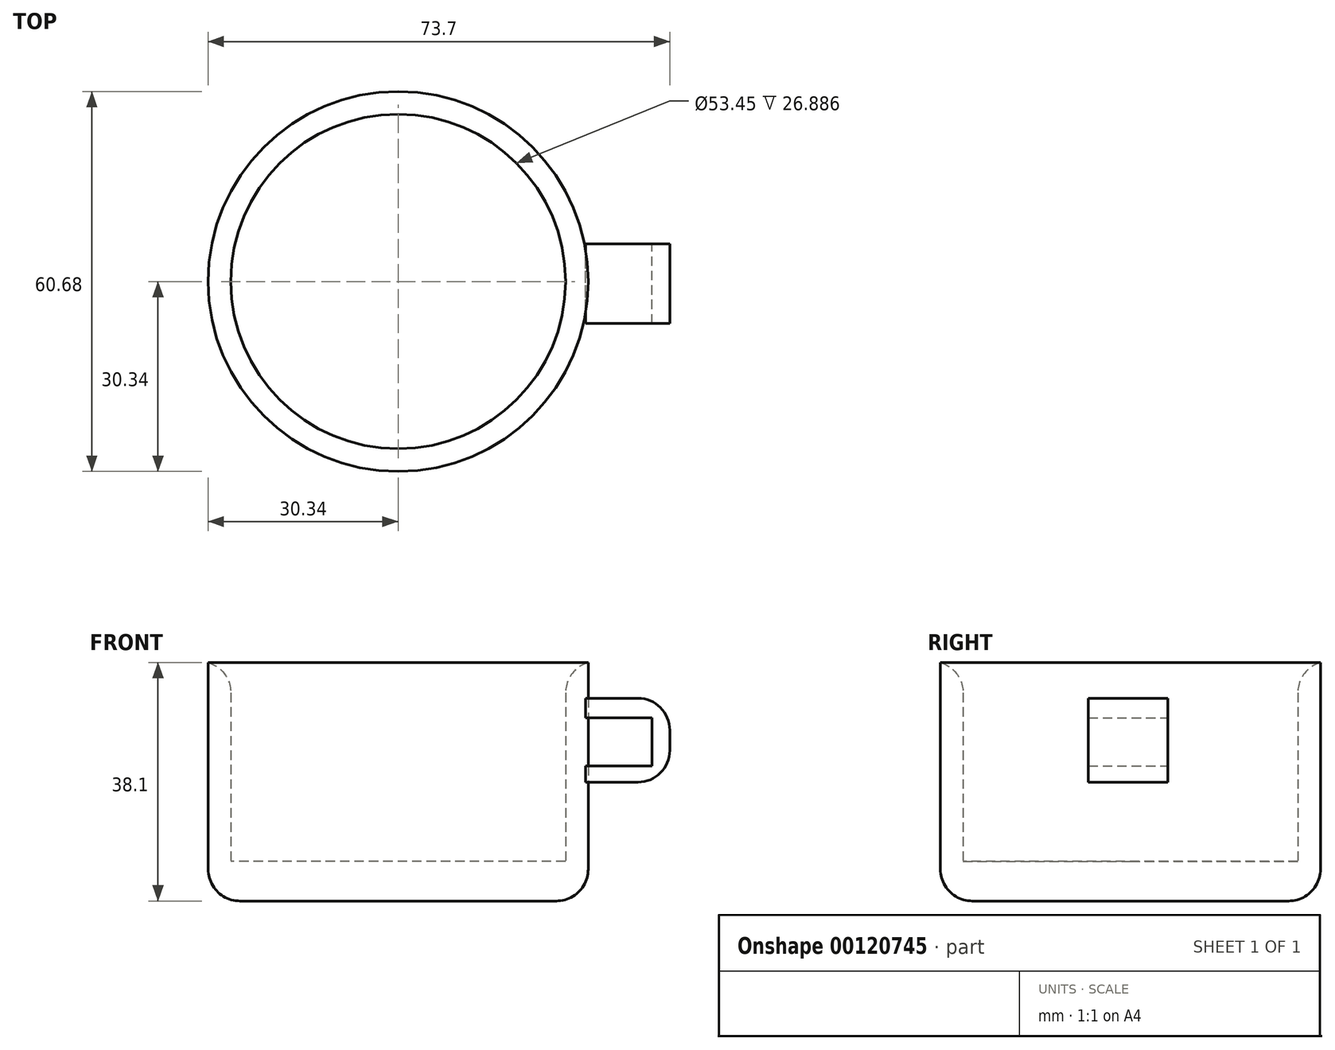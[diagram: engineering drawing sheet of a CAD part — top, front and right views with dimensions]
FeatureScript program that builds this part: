
annotation { "Feature Type Name" : "Feature", "Feature Type Description" : "" }
export const myFeature = defineFeature(function(context is Context, id is Id, definition is map)
    precondition{}
    {
        {
            var Q0;
            Q0=qCreatedBy(makeId("Top.planeOp"),FACE);
            var sketch = newSketch(context, id + "F0", { "sketchPlane" : qUnion([Q0])});
            skCircle(sketch, "E0", {"center": v(0, 0) * mm, "radius": 30.34 * mm});
            skCircle(sketch, "E1", {"center": v(0, 0) * mm, "radius": 26.72 * mm});
            skSolve(sketch);
        }
        {
            var Q0;
            Q0=makeQuery(id+"F0.imprint","IMPRINT",FACE,{"disambiguationData":[TD([[makeQuery(id+"F0.imprint","IMPRINT",EDGE,{"derivedFrom":sQuery(id+"F0.wireOp",EDGE,"E0")}),1.0]])]});
            extrude(context, id + "F1", {"entities" : qUnion([Q0]), "depth" : 38.1 * mm});
        }
        {
            var Q0;
            Q0=qCreatedBy(makeId("Top.planeOp"),FACE);
            var sketch = newSketch(context, id + "F2", { "sketchPlane" : qUnion([Q0])});
            skCircle(sketch, "E2", {"center": v(0, 0) * mm, "radius": 26.73 * mm});
            skSolve(sketch);
        }
        {
            var Q0;
            Q0 = qSketchRegion(id + "F2", true);
            extrude(context, id + "F3", {"entities" : qUnion([Q0]), "operationType" : NewBodyOperationType.ADD, "depth" : 6.35 * mm});
        }
        {
            var Q0;
            Q0=qCreatedBy(makeId("Front.planeOp"),FACE);
            var sketch = newSketch(context, id + "F4", { "sketchPlane" : qUnion([Q0])});
            skLineSegment(sketch, "E3", {"start": v(33.66, 32.37) * mm, "end": v(47.06, 32.37) * mm});
            skLineSegment(sketch, "E4", {"start": v(47.06, 32.37) * mm, "end": v(47.06, 18.97) * mm});
            skLineSegment(sketch, "E5", {"start": v(47.06, 18.97) * mm, "end": v(33.66, 18.97) * mm});
            skLineSegment(sketch, "E6", {"start": v(33.66, 18.97) * mm, "end": v(33.66, 21.54) * mm});
            skLineSegment(sketch, "E7", {"start": v(33.66, 21.54) * mm, "end": v(44.21, 21.54) * mm});
            skLineSegment(sketch, "E8", {"start": v(44.21, 21.54) * mm, "end": v(44.21, 29.24) * mm});
            skLineSegment(sketch, "E9", {"start": v(44.21, 29.24) * mm, "end": v(33.66, 29.24) * mm});
            skLineSegment(sketch, "E10", {"start": v(33.66, 29.24) * mm, "end": v(33.66, 32.37) * mm});
            skSolve(sketch);
        }
        {
            var Q0;
            Q0 = qSketchRegion(id + "F4", true);
            extrude(context, id + "F5", {"entities" : qUnion([Q0]), "depth" : 12.7 * mm});
        }
        {
            var Q0;
            Q0=makeQuery(id+"F5.opExtrude","SWEPT_BODY",BODY,{"disambiguationData":[OSD([sQuery(id+"F4.wireOp",EDGE,"E3"),sQuery(id+"F4.wireOp",EDGE,"E4"),sQuery(id+"F4.wireOp",EDGE,"E5"),sQuery(id+"F4.wireOp",EDGE,"E6"),sQuery(id+"F4.wireOp",EDGE,"E7"),sQuery(id+"F4.wireOp",EDGE,"E8"),sQuery(id+"F4.wireOp",EDGE,"E9"),sQuery(id+"F4.wireOp",EDGE,"E10")])]});
            transform(context, id + "F6", {"entities" : qUnion([Q0]), "transformType" : TransformType.TRANSLATION_3D, "dx" : -3.7 * mm, "dy" : 6 * mm, "dz" : 0 * mm, "makeCopy" : false});
        }
        {
            var Q0;
            Q0=makeQuery(id+"F1.opExtrude","CAP_EDGE",EDGE,{"disambiguationData":[OSD([sQuery(id+"F0.wireOp",EDGE,"E1")])],"isStart":false});
            var Q1;
            Q1=makeQuery(id+"F1.opExtrude","CAP_EDGE",EDGE,{"disambiguationData":[OSD([sQuery(id+"F0.wireOp",EDGE,"E0")])],"isStart":true});
            fillet(context, id + "F7", {"entities" : qUnion([Q0, Q1]), "radius" : 5.08 * mm, "tangentPropagation" : true, "allowEdgeOverflow" : false});
        }
        {
            var Q0;
            Q0=makeQuery(id+"F5.opExtrude","SWEPT_EDGE",EDGE,{"disambiguationData":[OSD([sQuery(id+"F4.wireOp",EDGE,"E3"),sQuery(id+"F4.wireOp",EDGE,"E4")])]});
            var Q1;
            Q1=makeQuery(id+"F5.opExtrude","SWEPT_EDGE",EDGE,{"disambiguationData":[OSD([sQuery(id+"F4.wireOp",EDGE,"E4"),sQuery(id+"F4.wireOp",EDGE,"E5")])]});
            fillet(context, id + "F8", {"entities" : qUnion([Q0, Q1]), "radius" : 5.08 * mm, "tangentPropagation" : true, "allowEdgeOverflow" : false});
        }
    });
